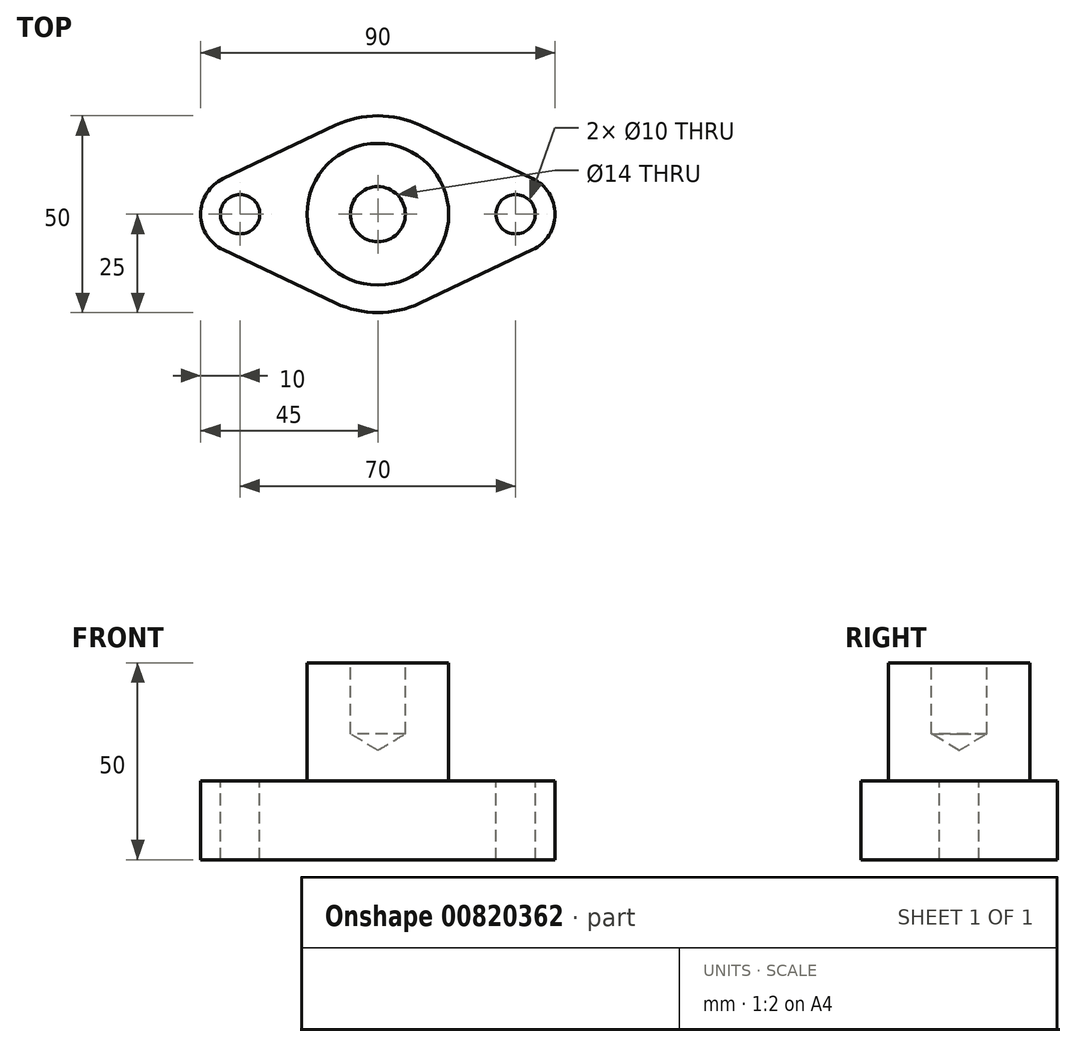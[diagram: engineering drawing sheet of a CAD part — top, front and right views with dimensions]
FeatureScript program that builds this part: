
annotation { "Feature Type Name" : "Feature", "Feature Type Description" : "" }
export const myFeature = defineFeature(function(context is Context, id is Id, definition is map)
    precondition{}
    {
        {
            var Q0;
            Q0=qCreatedBy(makeId("Top.planeOp"),FACE);
            var sketch = newSketch(context, id + "F0", { "sketchPlane" : qUnion([Q0])});
            skArc(sketch, "E0", {"start": v(10.71, 22.59) * mm, "mid": v(0, 25) * mm, "end": v(-10.71, 22.59) * mm});
            skArc(sketch, "E1", {"start": v(-39.29, 9.04) * mm, "mid": v(-45, 0) * mm, "end": v(-39.29, -9.04) * mm});
            skArc(sketch, "E2", {"start": v(39.29, -9.04) * mm, "mid": v(45, 0) * mm, "end": v(39.29, 9.04) * mm});
            skLineSegment(sketch, "E3", {"start": v(-39.29, 9.04) * mm, "end": v(-10.71, 22.59) * mm});
            skLineSegment(sketch, "E4", {"start": v(10.71, 22.59) * mm, "end": v(39.29, 9.04) * mm});
            skLineSegment(sketch, "E5", {"start": v(0, -27.67) * mm, "end": v(39.29, -9.04) * mm});
            skLineSegment(sketch, "E6", {"start": v(-39.29, -9.04) * mm, "end": v(0, -27.67) * mm});
            skArc(sketch, "E7", {"start": v(-10.71, -22.59) * mm, "mid": v(0, -25) * mm, "end": v(10.71, -22.59) * mm});
            skSolve(sketch);
        }
        {
            var Q0;
            {var subQ1=sQuery(id+"F0.wireOp",EDGE,"E1");Q0=makeQuery(id+"F0.imprint","IMPRINT",FACE,{"disambiguationData":[TD([[makeQuery(id+"F0.imprint","IMPRINT",EDGE,{"derivedFrom":subQ1}),1.0]])]});}
            extrude(context, id + "F1", {"entities" : qUnion([Q0]), "endBound" : BoundingType.SYMMETRIC, "depth" : 20 * mm, "offsetDistance" : 25 * mm});
        }
        {
            var Q0;
            Q0=makeQuery(id+"F1.opExtrude","CAP_FACE",FACE,{"disambiguationData":[OSD([sQuery(id+"F0.wireOp",EDGE,"E1"),sQuery(id+"F0.wireOp",EDGE,"E2"),sQuery(id+"F0.wireOp",EDGE,"E3"),sQuery(id+"F0.wireOp",EDGE,"E4"),sQuery(id+"F0.wireOp",EDGE,"E5"),sQuery(id+"F0.wireOp",EDGE,"E6"),sQuery(id+"F0.wireOp",EDGE,"E7"),sQuery(id+"F0.wireOp",EDGE,"E0")])],"isStart":false});
            var sketch = newSketch(context, id + "F2", { "sketchPlane" : qUnion([Q0])});
            skLineSegment(sketch, "E8", {"start": v(-45, 0) * mm, "end": v(-35, 0) * mm});
            skLineSegment(sketch, "E9", {"start": v(45, 0) * mm, "end": v(35, 0) * mm});
            skCircle(sketch, "E10", {"center": v(0, 0) * mm, "radius": 18 * mm});
            skSolve(sketch);
        }
        {
            var Q0;
            Q0=sQuery(id+"F2.wireOp",VERTEX,"E8.end");
            var Q1;
            Q1=sQuery(id+"F2.wireOp",VERTEX,"E9.end");
            var Q2;
            Q2=makeQuery(id+"F1.opExtrude","SWEPT_BODY",BODY,{"disambiguationData":[OSD([sQuery(id+"F0.wireOp",EDGE,"E1"),sQuery(id+"F0.wireOp",EDGE,"E2"),sQuery(id+"F0.wireOp",EDGE,"E3"),sQuery(id+"F0.wireOp",EDGE,"E4"),sQuery(id+"F0.wireOp",EDGE,"E5"),sQuery(id+"F0.wireOp",EDGE,"E6"),sQuery(id+"F0.wireOp",EDGE,"E7"),sQuery(id+"F0.wireOp",EDGE,"E0")])]});
            hole(context, id + "F3", {"style" : HoleStyle.SIMPLE, "endStyle" : HoleEndStyle.THROUGH, "holeDiameter" : 10 * mm, "majorDiameter" : 5 * mm, "isTappedThrough" : true, "tappedDepth" : 12 * mm, "tapClearance" : 3, "locations" : qUnion([Q0, Q1]), "scope" : qUnion([Q2])});
        }
        {
            var Q0;
            Q0=makeQuery(id+"F2.imprint","IMPRINT",FACE,{"disambiguationData":[TD([[makeQuery(id+"F2.imprint","IMPRINT",EDGE,{"derivedFrom":sQuery(id+"F2.wireOp",EDGE,"E10")}),1.0]])]});
            extrude(context, id + "F4", {"entities" : qUnion([Q0]), "operationType" : NewBodyOperationType.ADD, "depth" : 30 * mm, "offsetDistance" : 25 * mm});
        }
        {
            var Q0;
            Q0=makeQuery(id+"F4.opExtrude","CAP_FACE",FACE,{"disambiguationData":[OSD([sQuery(id+"F2.wireOp",EDGE,"E10")])],"isStart":false});
            var sketch = newSketch(context, id + "F5", { "sketchPlane" : qUnion([Q0])});
            skCircle(sketch, "E11", {"center": v(0, 0) * mm, "radius": 18 * mm});
            skSolve(sketch);
        }
        {
            var Q0;
            Q0=sQuery(id+"F5.wireOp",VERTEX,"E11.center");
            var Q1;
            Q1=makeQuery(id+"F1.opExtrude","SWEPT_BODY",BODY,{"disambiguationData":[OSD([sQuery(id+"F0.wireOp",EDGE,"E1"),sQuery(id+"F0.wireOp",EDGE,"E2"),sQuery(id+"F0.wireOp",EDGE,"E3"),sQuery(id+"F0.wireOp",EDGE,"E4"),sQuery(id+"F0.wireOp",EDGE,"E5"),sQuery(id+"F0.wireOp",EDGE,"E6"),sQuery(id+"F0.wireOp",EDGE,"E7"),sQuery(id+"F0.wireOp",EDGE,"E0")])]});
            hole(context, id + "F6", {"style" : HoleStyle.SIMPLE, "endStyle" : HoleEndStyle.BLIND, "standardTappedOrClearance" : lookupTablePath({ "standard" : "ISO", "engagement" : "75%", "pitch" : "2 mm", "size" : "M16", "type" : "Tapped" }), "standardBlindInLast" : lookupTablePath({ "standard" : "ISO", "engagement" : "75%", "pitch" : "2 mm", "size" : "M16", "type" : "Tapped" }), "holeDiameter" : 14 * mm, "majorDiameter" : 16 * mm, "showTappedDepth" : true, "holeDepth" : 18 * mm, "isTappedThrough" : true, "tappedDepth" : 12 * mm, "tapClearance" : 3, "locations" : qUnion([Q0]), "scope" : qUnion([Q1])});
        }
    });
